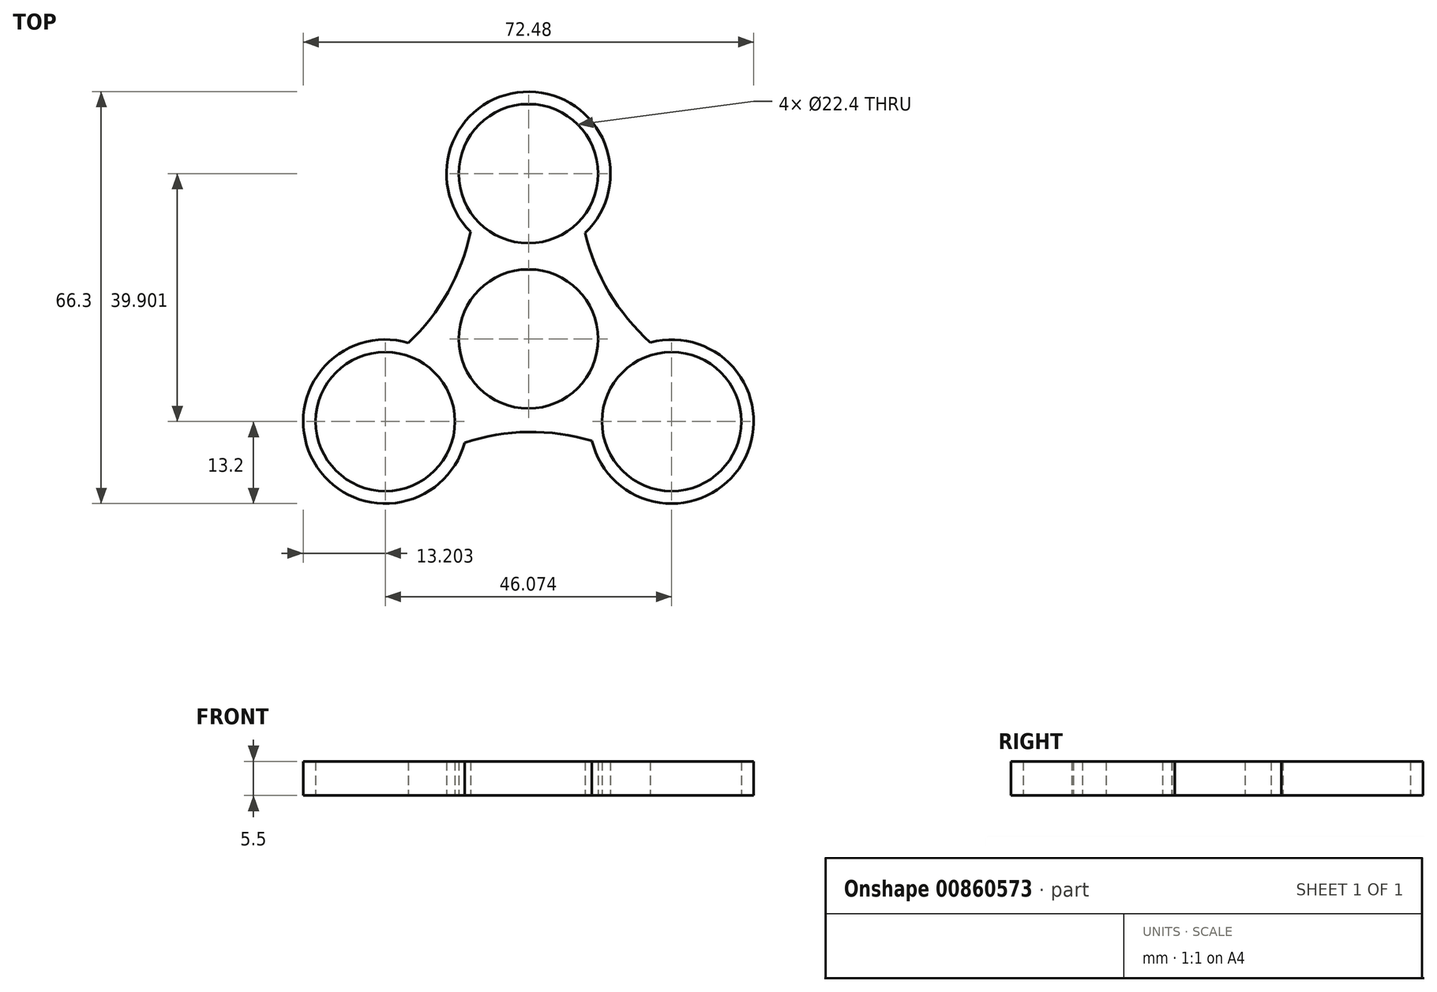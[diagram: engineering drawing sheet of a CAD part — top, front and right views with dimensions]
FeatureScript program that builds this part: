
annotation { "Feature Type Name" : "Feature", "Feature Type Description" : "" }
export const myFeature = defineFeature(function(context is Context, id is Id, definition is map)
    precondition{}
    {
        {
            var Q0;
            Q0=qCreatedBy(makeId("Top.planeOp"),FACE);
            var sketch = newSketch(context, id + "F0", { "sketchPlane" : qUnion([Q0])});
            skCircle(sketch, "E0", {"center": v(0, 0) * mm, "radius": 11.2 * mm});
            skCircle(sketch, "E1", {"center": v(0, 26.6) * mm, "radius": 11.2 * mm});
            skCircle(sketch, "E2", {"center": v(0, 26.6) * mm, "radius": 13.2 * mm});
            skCircle(sketch, "E3.1.0", {"center": v(-23.04, -13.3) * mm, "radius": 11.2 * mm});
            skCircle(sketch, "E3.1.1", {"center": v(-23.04, -13.3) * mm, "radius": 13.2 * mm});
            skCircle(sketch, "E3.2.0", {"center": v(23.04, -13.3) * mm, "radius": 11.2 * mm});
            skCircle(sketch, "E3.2.1", {"center": v(23.04, -13.3) * mm, "radius": 13.2 * mm});
            skArc(sketch, "E4", {"start": v(9.1, 17.05) * mm, "mid": v(13, 7.44) * mm, "end": v(19.61, -0.55) * mm});
            skArc(sketch, "E5.1.0", {"start": v(-19.32, -0.64) * mm, "mid": v(-12.94, 7.54) * mm, "end": v(-9.33, 17.26) * mm});
            skArc(sketch, "E5.2.0", {"start": v(10.2, -16.41) * mm, "mid": v(-0.06, -14.98) * mm, "end": v(-10.28, -16.7) * mm});
            skSolve(sketch);
        }
        {
            var Q0;
            Q0=makeQuery(id+"F0.imprint","IMPRINT",FACE,{"disambiguationData":[TD([[makeQuery(id+"F0.imprint","IMPRINT",EDGE,{"derivedFrom":sQuery(id+"F0.wireOp",EDGE,"E0")}),-1.0]])]});
            var Q1;
            Q1=makeQuery(id+"F0.imprint","IMPRINT",FACE,{"disambiguationData":[TD([[makeQuery(id+"F0.imprint","IMPRINT",EDGE,{"derivedFrom":sQuery(id+"F0.wireOp",EDGE,"E3.2.0")}),-1.0]])]});
            var Q2;
            Q2=makeQuery(id+"F0.imprint","IMPRINT",FACE,{"disambiguationData":[TD([[makeQuery(id+"F0.imprint","IMPRINT",EDGE,{"derivedFrom":sQuery(id+"F0.wireOp",EDGE,"E1")}),-1.0]])]});
            var Q3;
            Q3=makeQuery(id+"F0.imprint","IMPRINT",FACE,{"disambiguationData":[TD([[makeQuery(id+"F0.imprint","IMPRINT",EDGE,{"derivedFrom":sQuery(id+"F0.wireOp",EDGE,"E3.1.0")}),-1.0]])]});
            extrude(context, id + "F1", {"entities" : qUnion([Q0, Q1, Q2, Q3]), "depth" : 5.5 * mm, "offsetDistance" : 25 * mm});
        }
    });
